# Revit family: РИДАН_RJIP Premium FB_FF_H DN15-125
name_source: partatom
category: Арматура трубопроводов
units: mm (PartAtom-declared; Revit-internal decimal feet)

## family parameters
Всегда вертикально = Да
На основе рабочей плоскости = Нет
Общий = Нет
При загрузке вырезать с полостями = Нет
Размер круглого соединителя = Использовать диаметр
Тип детали = Вставляется

## types (14) — shared parameters
ADSK_Версия Revit = 2019
ADSK_Версия семейства = 1.0
ADSK_Единица измерения = шт.
ADSK_Завод-изготовитель = ООО «Ридан-Трейд»
ADSK_Количество = 1
ADSK_Потеря давления жидкости = 0.0 Па
ADSK_Расход жидкости = 0 м³/ч
LT = Table
URL = https://ridan.ru
Изготовитель = ООО «Ридан-Трейд»

## per-type parameters (varying)
| type | ADSK_Диаметр условный | ADSK_Код изделия | ADSK_Марка | ADSK_Масса | ADSK_Наименование | ADSK_Пропускная способность | a | b | c | d | e | f | g | h | i | j | k | l | m | n | num |
| DN 15 PN40 | 15 мм | 065N1300R | RJIP Premium FB FF DN15 PN40 H | 2.1 | RJIP Premium Кран шаровой FB FF DN15 PN40 H (фланцевый, с рукояткой, полнопроходной) | 18 м³/ч | 31 мм | 12 мм | 100 мм | 50 мм | 21 мм | 42 мм | 73 мм | 27 мм | 213 мм | 12 мм | 95 мм | 50 мм | 46 мм | 2 мм | 1 |
| DN 20 PN40 | 20 мм | 065N1305R | RJIP Premium FB FF DN20 PN40 H | 2.39 | RJIP Premium Кран шаровой FB FF DN20 PN40 H (фланцевый, с рукояткой, полнопроходной) | 46 м³/ч | 31 мм | 22 мм | 100 мм | 50 мм | 27 мм | 48 мм | 76 мм | 27 мм | 238 мм | 14 мм | 105 мм | 58 мм | 54 мм | 2 мм | 2 |
| DN 25 PN40 | 25 мм | 065N1310R | RJIP Premium FB FF DN25 PN40 H | 2.94 | RJIP Premium Кран шаровой FB FF DN25 PN40 H (фланцевый, с рукояткой, полнопроходной) | 71 м³/ч | 29 мм | 39 мм | 100 мм | 50 мм | 34 мм | 57 мм | 81 мм | 27 мм | 268 мм | 14 мм | 115 мм | 68 мм | 64 мм | 2 мм | 3 |
| DN 32 PN40 | 32 мм | 065N1315R | RJIP Premium FB FF DN32 PN40 H | 5.9 | RJIP Premium Кран шаровой FB FF DN32 PN40 H (фланцевый, с рукояткой, полнопроходной) | 79 м³/ч | 28 мм | 48 мм | 120 мм | 60 мм | 42 мм | 76 мм | 87 мм | 34 мм | 308 мм | 16 мм | 140 мм | 78 мм | 74 мм | 2 мм | 4 |
| DN 40 PN40 | 40 мм | 065N1320R | RJIP Premium FB FF DN40 PN40 H | 6.49 | RJIP Premium Кран шаровой FB FF DN40 PN40 H (фланцевый, с рукояткой, полнопроходной) | 125 м³/ч | 27 мм | 40 мм | 137 мм | 69 мм | 48 мм | 89 мм | 93 мм | 34 мм | 308 мм | 15 мм | 150 мм | 92 мм | 86 мм | 3 мм | 5 |
| DN 50 PN40 | 50 мм | 065N1325R | RJIP Premium FB FF DN50 PN40 H | 9 | RJIP Premium Кран шаровой FB FF DN50 PN40 H (фланцевый, с рукояткой, полнопроходной) | 189 м³/ч | 28 мм | 46 мм | 120 мм | 60 мм | 60 мм | 114 мм | 108 мм | 34 мм | 308 мм | 17 мм | 165 мм | 106 мм | 100 мм | 3 мм | 6 |
| DN 65 PN25 | 65 мм | 065N1330R | RJIP Premium FB FF DN65 PN25 H | 13.21 | RJIP Premium Кран шаровой FB FF DN65 PN25 H (фланцевый, с рукояткой, полнопроходной) | 328 м³/ч | 25 мм | 36 мм | 150 мм | 75 мм | 76 мм | 140 мм | 124 мм | 39 мм | 320 мм | 21 мм | 180 мм | 128 мм | 122 мм | 3 мм | 7 |
| DN 80 PN25 | 80 мм | 065N1335R | RJIP Premium FB FF DN80 PN25 H | 20 | RJIP Premium Кран шаровой FB FF DN80 PN25 H (фланцевый, с рукояткой, полнопроходной) | 494 м³/ч | 19 мм | 50 мм | 160 мм | 80 мм | 89 мм | 159 мм | 136 мм | 39 мм | 345 мм | 21 мм | 195 мм | 139 мм | 133 мм | 3 мм | 8 |
| DN 100 PN25 | 100 мм | 065N1940R | RJIP Premium FB FF DN100 PN25 H | 24 | RJIP Premium Кран шаровой FB FF DN100 PN25 H (фланцевый, с рукояткой, полнопроходной) | 1358 м³/ч | 9 мм | 44 мм | 183 мм | 92 мм | 108 мм | 180 мм | 150 мм | 49 мм | 340 мм | 23 мм | 198 мм | 114 мм | 110 мм | 3 мм | 9 |
| DN 125 PN25 | 125 мм | 065N1945R | RJIP Premium FB FF DN125 PN25 H | 34.45 | RJIP Premium Кран шаровой FB FF DN125 PN25 H (фланцевый, с рукояткой, полнопроходной) | 2156 м³/ч | 18 мм | 29 мм | 220 мм | 110 мм | 133 мм | 219 мм | 172 мм | 49 мм | 370 мм | 25 мм | 245 мм | 133 мм | 128 мм | 3 мм | 10 |
| DN 65 PN16 | 65 мм | 065N1230R | RJIP Premium FB FF DN65 PN16 H | 8 | RJIP Premium Кран шаровой FB FF DN65 PN16 H (фланцевый, с рукояткой, полнопроходной) | 328 м³/ч | 24 мм | 36 мм | 150 мм | 75 мм | 76 мм | 140 мм | 124 мм | 39 мм | 310 мм | 17 мм | 185 мм | 126 мм | 120 мм | 3 мм | 11 |
| DN 80 PN16 | 80 мм | 065N1235R | RJIP Premium FB FF DN80 PN16 H | 18 | RJIP Premium Кран шаровой FB FF DN80 PN16 H (фланцевый, с рукояткой, полнопроходной) | 494 м³/ч | 19 мм | 50 мм | 160 мм | 80 мм | 89 мм | 159 мм | 136 мм | 39 мм | 337 мм | 17 мм | 200 мм | 140 мм | 134 мм | 3 мм | 12 |
| DN 100 PN16 | 100 мм | 065N1840R | RJIP Premium FB FF DN100 PN16 H | 13 | RJIP Premium Кран шаровой FB FF DN100 PN16 H (фланцевый, с рукояткой, полнопроходной) | 1358 м³/ч | 9 мм | 44 мм | 183 мм | 92 мм | 108 мм | 180 мм | 150 мм | 49 мм | 332 мм | 19 мм | 220 мм | 111 мм | 107 мм | 3 мм | 13 |
| DN 125 PN16 | 125 мм | 065N1845R | RJIP Premium FB FF DN125 PN16 H | 31.76 | RJIP Premium Кран шаровой FB FF DN125 PN16 H (фланцевый, с рукояткой, полнопроходной) | 2156 м³/ч | 22 мм | 29 мм | 220 мм | 110 мм | 133 мм | 219 мм | 172 мм | 49 мм | 366 мм | 19 мм | 250 мм | 192 мм | 186 мм | 3 мм | 14 |
